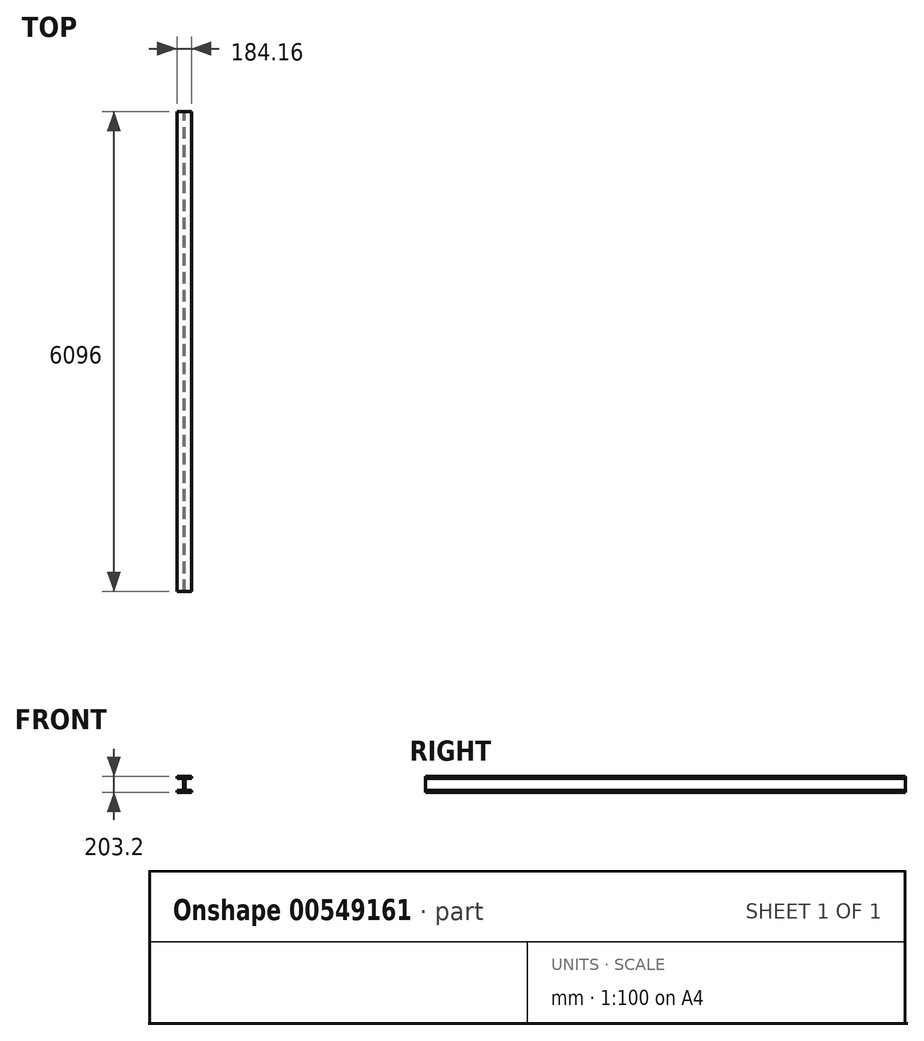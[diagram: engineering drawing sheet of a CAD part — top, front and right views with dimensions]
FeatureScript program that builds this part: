
annotation { "Feature Type Name" : "Feature", "Feature Type Description" : "" }
export const myFeature = defineFeature(function(context is Context, id is Id, definition is map)
    precondition{}
    {
        {
            var Q0;
            Q0=qCreatedBy(makeId("Front.planeOp"),FACE);
            var sketch = newSketch(context, id + "F0", { "sketchPlane" : qUnion([Q0])});
            skLineSegment(sketch, "E0", {"start": v(92.08, -76.2) * mm, "end": v(12.07, -76.2) * mm});
            skLineSegment(sketch, "E1", {"start": v(9.52, -73.66) * mm, "end": v(9.52, 73.66) * mm});
            skLineSegment(sketch, "E2", {"start": v(12.07, 76.2) * mm, "end": v(92.08, 76.2) * mm});
            skLineSegment(sketch, "E3", {"start": v(-92.08, 76.2) * mm, "end": v(-12.07, 76.2) * mm});
            skLineSegment(sketch, "E4", {"start": v(-9.53, 73.66) * mm, "end": v(-9.53, -73.66) * mm});
            skLineSegment(sketch, "E5", {"start": v(-12.06, -76.2) * mm, "end": v(-92.08, -76.2) * mm});
            skLineSegment(sketch, "E6", {"start": v(0, 0) * mm, "end": v(-9.52, 0) * mm, "construction": true});
            skLineSegment(sketch, "E7", {"start": v(0, 0) * mm, "end": v(9.52, 0) * mm, "construction": true});
            skLineSegment(sketch, "E8", {"start": v(0, 0) * mm, "end": v(0, 101.6) * mm, "construction": true});
            skLineSegment(sketch, "E9", {"start": v(0, 0) * mm, "end": v(0, -101.6) * mm, "construction": true});
            skPoint(sketch, "E10.visualSharp", {"position": v(-9.53, 76.2) * mm});
            skArc(sketch, "E10.filletArc", {"start": v(-9.52, 73.66) * mm, "mid": v(-10.27, 75.46) * mm, "end": v(-12.07, 76.2) * mm});
            skPoint(sketch, "E11.visualSharp", {"position": v(9.53, 76.2) * mm});
            skArc(sketch, "E11.filletArc", {"start": v(12.07, 76.2) * mm, "mid": v(10.27, 75.46) * mm, "end": v(9.52, 73.66) * mm});
            skPoint(sketch, "E12.visualSharp", {"position": v(9.53, -76.2) * mm});
            skArc(sketch, "E12.filletArc", {"start": v(9.52, -73.66) * mm, "mid": v(10.27, -75.46) * mm, "end": v(12.07, -76.2) * mm});
            skPoint(sketch, "E13.visualSharp", {"position": v(-9.53, -76.2) * mm});
            skArc(sketch, "E13.filletArc", {"start": v(-12.06, -76.2) * mm, "mid": v(-10.27, -75.46) * mm, "end": v(-9.52, -73.66) * mm});
            skPoint(sketch, "E14.visualSharp", {"position": v(-92.08, 101.6) * mm});
            skPoint(sketch, "E15.visualSharp", {"position": v(92.08, 101.6) * mm});
            skPoint(sketch, "E16.visualSharp", {"position": v(92.08, 76.2) * mm});
            skPoint(sketch, "E17.visualSharp", {"position": v(92.08, -101.6) * mm});
            skPoint(sketch, "E18.visualSharp", {"position": v(-92.08, -76.2) * mm});
            skPoint(sketch, "E19.visualSharp", {"position": v(-92.08, -101.6) * mm});
            skLineSegment(sketch, "E20", {"start": v(92.08, -76.2) * mm, "end": v(92.08, -101.6) * mm});
            skLineSegment(sketch, "E21", {"start": v(-92.08, -76.2) * mm, "end": v(-92.08, -101.6) * mm});
            skLineSegment(sketch, "E22", {"start": v(-92.08, 101.6) * mm, "end": v(-92.08, 76.2) * mm});
            skLineSegment(sketch, "E23", {"start": v(92.08, 101.6) * mm, "end": v(92.08, 76.2) * mm});
            skLineSegment(sketch, "E24", {"start": v(-92.08, 101.6) * mm, "end": v(92.08, 101.6) * mm});
            skLineSegment(sketch, "E25", {"start": v(-92.07, -101.6) * mm, "end": v(92.08, -101.6) * mm});
            skSolve(sketch);
        }
        {
            var Q0;
            Q0=makeQuery(id+"F0.imprint","IMPRINT",FACE,{"disambiguationData":[TD([[makeQuery(id+"F0.imprint","IMPRINT",EDGE,{"derivedFrom":sQuery(id+"F0.wireOp",EDGE,"E0")}),1.0]])]});
            extrude(context, id + "F1", {"entities" : qUnion([Q0]), "endBound" : BoundingType.SYMMETRIC, "depth" : 6096 * mm});
        }
    });
